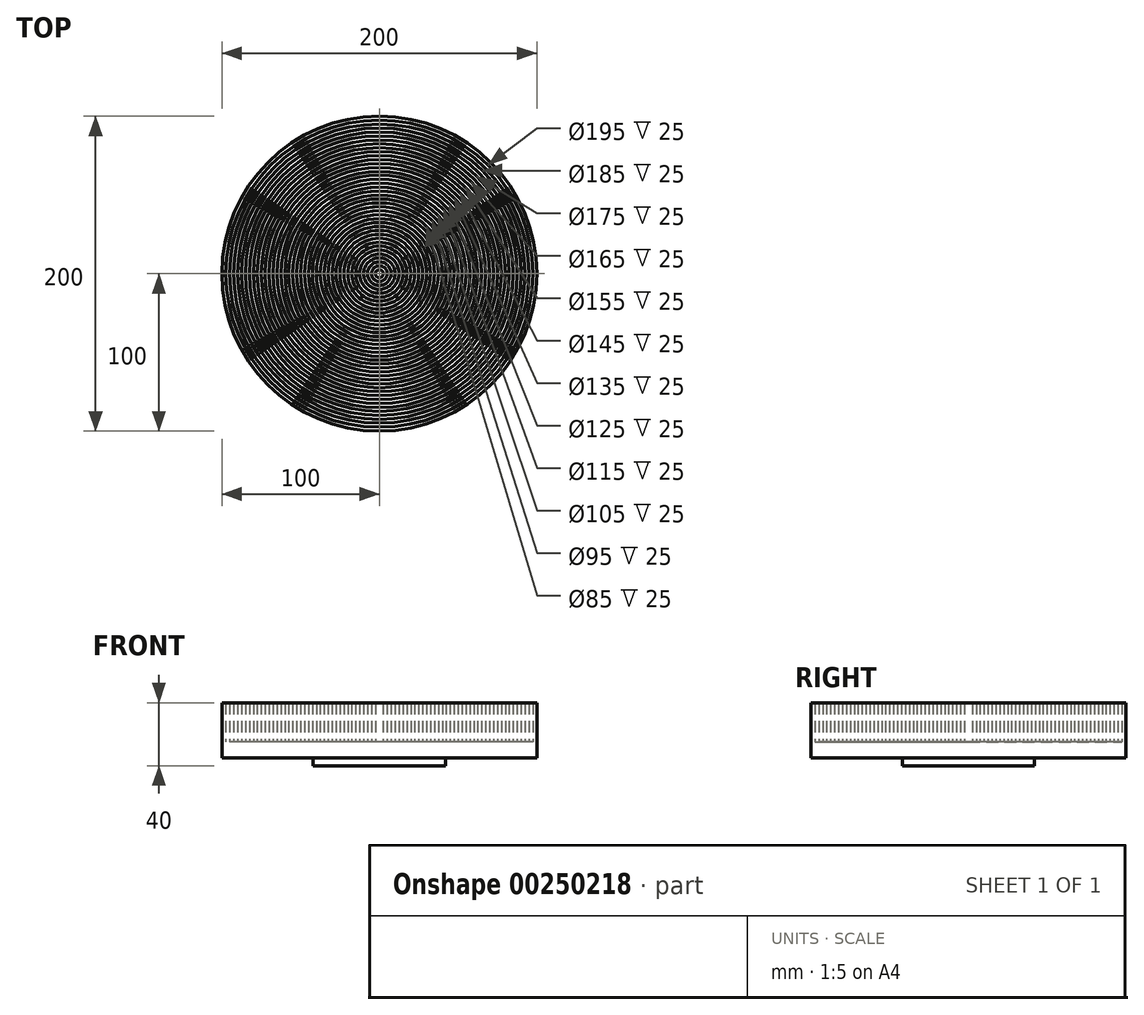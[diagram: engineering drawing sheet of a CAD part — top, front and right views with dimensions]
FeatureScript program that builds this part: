
annotation { "Feature Type Name" : "Feature", "Feature Type Description" : "" }
export const myFeature = defineFeature(function(context is Context, id is Id, definition is map)
    precondition{}
    {
        {
            var Q0;
            Q0=qCreatedBy(makeId("Top.planeOp"),FACE);
            var sketch = newSketch(context, id + "F0", { "sketchPlane" : qUnion([Q0])});
            skCircle(sketch, "E0", {"center": v(0, 0) * mm, "radius": 100 * mm});
            skSolve(sketch);
        }
        {
            var Q0;
            Q0=makeQuery(id+"F0.imprint","IMPRINT",FACE,{"disambiguationData":[TD([[makeQuery(id+"F0.imprint","IMPRINT",EDGE,{"derivedFrom":sQuery(id+"F0.wireOp",EDGE,"E0")}),1.0]])]});
            extrude(context, id + "F1", {"entities" : qUnion([Q0]), "depth" : 10 * mm});
        }
        {
            var Q0;
            Q0=makeQuery(id+"F1.opExtrude","CAP_FACE",FACE,{"disambiguationData":[OSD([sQuery(id+"F0.wireOp",EDGE,"E0")])],"isStart":false});
            var sketch = newSketch(context, id + "F2", { "sketchPlane" : qUnion([Q0])});
            skCircle(sketch, "E1", {"center": v(0, 0) * mm, "radius": 97.5 * mm});
            skCircle(sketch, "E2", {"center": v(0, 0) * mm, "radius": 95 * mm});
            skCircle(sketch, "E3", {"center": v(0, 0) * mm, "radius": 92.5 * mm});
            skCircle(sketch, "E4", {"center": v(0, 0) * mm, "radius": 90 * mm});
            skCircle(sketch, "E5", {"center": v(0, 0) * mm, "radius": 87.5 * mm});
            skCircle(sketch, "E6", {"center": v(0, 0) * mm, "radius": 85 * mm});
            skCircle(sketch, "E7", {"center": v(0, 0) * mm, "radius": 82.5 * mm});
            skCircle(sketch, "E8", {"center": v(0, 0) * mm, "radius": 80 * mm});
            skCircle(sketch, "E9", {"center": v(0, 0) * mm, "radius": 77.5 * mm});
            skCircle(sketch, "E10", {"center": v(0, 0) * mm, "radius": 75 * mm});
            skCircle(sketch, "E11", {"center": v(0, 0) * mm, "radius": 72.5 * mm});
            skCircle(sketch, "E12", {"center": v(0, 0) * mm, "radius": 70 * mm});
            skCircle(sketch, "E13", {"center": v(0, 0) * mm, "radius": 67.5 * mm});
            skCircle(sketch, "E14", {"center": v(0, 0) * mm, "radius": 65 * mm});
            skCircle(sketch, "E15", {"center": v(0, 0) * mm, "radius": 62.5 * mm});
            skCircle(sketch, "E16", {"center": v(0, 0) * mm, "radius": 60 * mm});
            skCircle(sketch, "E17", {"center": v(0, 0) * mm, "radius": 57.5 * mm});
            skCircle(sketch, "E18", {"center": v(0, 0) * mm, "radius": 55 * mm});
            skCircle(sketch, "E19", {"center": v(0, 0) * mm, "radius": 52.5 * mm});
            skCircle(sketch, "E20", {"center": v(0, 0) * mm, "radius": 50 * mm});
            skCircle(sketch, "E21", {"center": v(0, 0) * mm, "radius": 47.5 * mm});
            skCircle(sketch, "E22", {"center": v(0, 0) * mm, "radius": 45 * mm});
            skCircle(sketch, "E23", {"center": v(0, 0) * mm, "radius": 42.5 * mm});
            skCircle(sketch, "E24", {"center": v(0, 0) * mm, "radius": 40 * mm});
            skCircle(sketch, "E25", {"center": v(0, 0) * mm, "radius": 37.5 * mm});
            skCircle(sketch, "E26", {"center": v(0, 0) * mm, "radius": 35 * mm});
            skCircle(sketch, "E27", {"center": v(0, 0) * mm, "radius": 32.5 * mm});
            skCircle(sketch, "E28", {"center": v(0, 0) * mm, "radius": 30 * mm});
            skCircle(sketch, "E29", {"center": v(0, 0) * mm, "radius": 27.5 * mm});
            skCircle(sketch, "E30", {"center": v(0, 0) * mm, "radius": 25 * mm});
            skCircle(sketch, "E31", {"center": v(0, 0) * mm, "radius": 22.5 * mm});
            skCircle(sketch, "E32", {"center": v(0, 0) * mm, "radius": 20 * mm});
            skCircle(sketch, "E33", {"center": v(0, 0) * mm, "radius": 17.5 * mm});
            skCircle(sketch, "E34", {"center": v(0, 0) * mm, "radius": 15 * mm});
            skCircle(sketch, "E35", {"center": v(0, 0) * mm, "radius": 12.5 * mm});
            skCircle(sketch, "E36", {"center": v(0, 0) * mm, "radius": 10 * mm});
            skCircle(sketch, "E37", {"center": v(0, 0) * mm, "radius": 7.5 * mm});
            skCircle(sketch, "E38", {"center": v(0, 0) * mm, "radius": 5 * mm});
            skCircle(sketch, "E39", {"center": v(0, 0) * mm, "radius": 2.5 * mm});
            skSolve(sketch);
        }
        {
            var Q0;
            Q0=makeQuery(id+"F2.imprint","IMPRINT",FACE,{"disambiguationData":[TD([[makeQuery(id+"F2.imprint","IMPRINT",EDGE,{"derivedFrom":sQuery(id+"F2.wireOp",EDGE,"E1")}),-1.0]])]});
            var Q1;
            Q1=makeQuery(id+"F2.imprint","IMPRINT",FACE,{"disambiguationData":[TD([[makeQuery(id+"F2.imprint","IMPRINT",EDGE,{"derivedFrom":sQuery(id+"F2.wireOp",EDGE,"E2")}),1.0]])]});
            var Q2;
            Q2=makeQuery(id+"F2.imprint","IMPRINT",FACE,{"disambiguationData":[TD([[makeQuery(id+"F2.imprint","IMPRINT",EDGE,{"derivedFrom":sQuery(id+"F2.wireOp",EDGE,"E4")}),1.0]])]});
            var Q3;
            Q3=makeQuery(id+"F2.imprint","IMPRINT",FACE,{"disambiguationData":[TD([[makeQuery(id+"F2.imprint","IMPRINT",EDGE,{"derivedFrom":sQuery(id+"F2.wireOp",EDGE,"E6")}),1.0]])]});
            var Q4;
            Q4=makeQuery(id+"F2.imprint","IMPRINT",FACE,{"disambiguationData":[TD([[makeQuery(id+"F2.imprint","IMPRINT",EDGE,{"derivedFrom":sQuery(id+"F2.wireOp",EDGE,"E8")}),1.0]])]});
            var Q5;
            Q5=makeQuery(id+"F2.imprint","IMPRINT",FACE,{"disambiguationData":[TD([[makeQuery(id+"F2.imprint","IMPRINT",EDGE,{"derivedFrom":sQuery(id+"F2.wireOp",EDGE,"E10")}),1.0]])]});
            var Q6;
            Q6=makeQuery(id+"F2.imprint","IMPRINT",FACE,{"disambiguationData":[TD([[makeQuery(id+"F2.imprint","IMPRINT",EDGE,{"derivedFrom":sQuery(id+"F2.wireOp",EDGE,"E12")}),1.0]])]});
            var Q7;
            Q7=makeQuery(id+"F2.imprint","IMPRINT",FACE,{"disambiguationData":[TD([[makeQuery(id+"F2.imprint","IMPRINT",EDGE,{"derivedFrom":sQuery(id+"F2.wireOp",EDGE,"E14")}),1.0]])]});
            var Q8;
            Q8=makeQuery(id+"F2.imprint","IMPRINT",FACE,{"disambiguationData":[TD([[makeQuery(id+"F2.imprint","IMPRINT",EDGE,{"derivedFrom":sQuery(id+"F2.wireOp",EDGE,"E16")}),1.0]])]});
            var Q9;
            Q9=makeQuery(id+"F2.imprint","IMPRINT",FACE,{"disambiguationData":[TD([[makeQuery(id+"F2.imprint","IMPRINT",EDGE,{"derivedFrom":sQuery(id+"F2.wireOp",EDGE,"E18")}),1.0]])]});
            var Q10;
            Q10=makeQuery(id+"F2.imprint","IMPRINT",FACE,{"disambiguationData":[TD([[makeQuery(id+"F2.imprint","IMPRINT",EDGE,{"derivedFrom":sQuery(id+"F2.wireOp",EDGE,"E20")}),1.0]])]});
            var Q11;
            Q11=makeQuery(id+"F2.imprint","IMPRINT",FACE,{"disambiguationData":[TD([[makeQuery(id+"F2.imprint","IMPRINT",EDGE,{"derivedFrom":sQuery(id+"F2.wireOp",EDGE,"E22")}),1.0]])]});
            var Q12;
            Q12=makeQuery(id+"F2.imprint","IMPRINT",FACE,{"disambiguationData":[TD([[makeQuery(id+"F2.imprint","IMPRINT",EDGE,{"derivedFrom":sQuery(id+"F2.wireOp",EDGE,"E24")}),1.0]])]});
            var Q13;
            Q13=makeQuery(id+"F2.imprint","IMPRINT",FACE,{"disambiguationData":[TD([[makeQuery(id+"F2.imprint","IMPRINT",EDGE,{"derivedFrom":sQuery(id+"F2.wireOp",EDGE,"E26")}),1.0]])]});
            var Q14;
            Q14=makeQuery(id+"F2.imprint","IMPRINT",FACE,{"disambiguationData":[TD([[makeQuery(id+"F2.imprint","IMPRINT",EDGE,{"derivedFrom":sQuery(id+"F2.wireOp",EDGE,"E28")}),1.0]])]});
            var Q15;
            Q15=makeQuery(id+"F2.imprint","IMPRINT",FACE,{"disambiguationData":[TD([[makeQuery(id+"F2.imprint","IMPRINT",EDGE,{"derivedFrom":sQuery(id+"F2.wireOp",EDGE,"E30")}),1.0]])]});
            var Q16;
            Q16=makeQuery(id+"F2.imprint","IMPRINT",FACE,{"disambiguationData":[TD([[makeQuery(id+"F2.imprint","IMPRINT",EDGE,{"derivedFrom":sQuery(id+"F2.wireOp",EDGE,"E32")}),1.0]])]});
            var Q17;
            Q17=makeQuery(id+"F2.imprint","IMPRINT",FACE,{"disambiguationData":[TD([[makeQuery(id+"F2.imprint","IMPRINT",EDGE,{"derivedFrom":sQuery(id+"F2.wireOp",EDGE,"E34")}),1.0]])]});
            var Q18;
            Q18=makeQuery(id+"F2.imprint","IMPRINT",FACE,{"disambiguationData":[TD([[makeQuery(id+"F2.imprint","IMPRINT",EDGE,{"derivedFrom":sQuery(id+"F2.wireOp",EDGE,"E36")}),1.0]])]});
            var Q19;
            Q19=makeQuery(id+"F2.imprint","IMPRINT",FACE,{"disambiguationData":[TD([[makeQuery(id+"F2.imprint","IMPRINT",EDGE,{"derivedFrom":sQuery(id+"F2.wireOp",EDGE,"E38")}),1.0]])]});
            extrude(context, id + "F3", {"entities" : qUnion([Q0, Q1, Q2, Q3, Q4, Q5, Q6, Q7, Q8, Q9, Q10, Q11, Q12, Q13, Q14, Q15, Q16, Q17, Q18, Q19]), "operationType" : NewBodyOperationType.ADD, "depth" : 25 * mm});
        }
        {
            var Q0;
            Q0=makeQuery(id+"F1.opExtrude","CAP_FACE",FACE,{"disambiguationData":[OSD([sQuery(id+"F0.wireOp",EDGE,"E0")])],"isStart":true});
            var sketch = newSketch(context, id + "F4", { "sketchPlane" : qUnion([Q0])});
            skCircle(sketch, "E40", {"center": v(0, 0) * mm, "radius": 41.97 * mm});
            skSolve(sketch);
        }
        {
            var Q0;
            Q0 = qSketchRegion(id + "F4", true);
            extrude(context, id + "F5", {"entities" : qUnion([Q0]), "operationType" : NewBodyOperationType.ADD, "depth" : 5 * mm});
        }
    });
